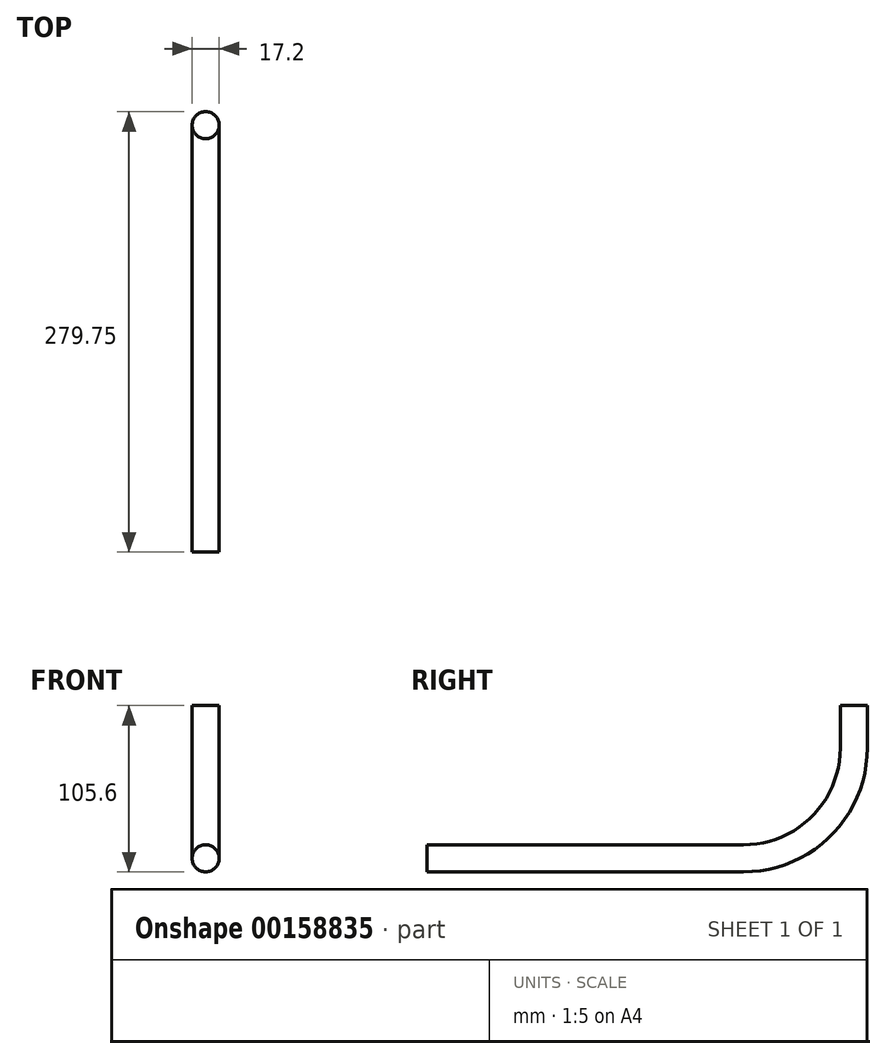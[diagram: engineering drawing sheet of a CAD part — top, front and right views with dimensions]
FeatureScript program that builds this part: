
annotation { "Feature Type Name" : "Feature", "Feature Type Description" : "" }
export const myFeature = defineFeature(function(context is Context, id is Id, definition is map)
    precondition{}
    {
        {
            var Q0;
            Q0=qCreatedBy(makeId("Right.planeOp"),FACE);
            var sketch = newSketch(context, id + "F0", { "sketchPlane" : qUnion([Q0])});
            skLineSegment(sketch, "E0", {"start": v(0, 0) * mm, "end": v(0, -27) * mm});
            skLineSegment(sketch, "E1", {"start": v(-70, -97) * mm, "end": v(-271.15, -97) * mm});
            skPoint(sketch, "E2.visualSharp", {"position": v(0, -97) * mm});
            skArc(sketch, "E2.filletArc", {"start": v(-70, -97) * mm, "mid": v(-20.5, -76.5) * mm, "end": v(0, -27) * mm});
            skSolve(sketch);
        }
        {
            var Q0;
            Q0=qCreatedBy(makeId("Top.planeOp"),FACE);
            var sketch = newSketch(context, id + "F1", { "sketchPlane" : qUnion([Q0])});
            skCircle(sketch, "E3", {"center": v(0, 0) * mm, "radius": 8.6 * mm});
            skSolve(sketch);
        }
        {
            var Q0;
            Q0=makeQuery(id+"F1.imprint","IMPRINT",FACE,{"disambiguationData":[TD([[makeQuery(id+"F1.imprint","IMPRINT",EDGE,{"derivedFrom":sQuery(id+"F1.wireOp",EDGE,"E3")}),1.0]])]});
            var Q1;
            Q1=sQuery(id+"F0.wireOp",EDGE,"E0");
            var Q2;
            Q2=sQuery(id+"F0.wireOp",EDGE,"E2.filletArc");
            var Q3;
            Q3=sQuery(id+"F0.wireOp",EDGE,"E1");
            sweep(context, id + "F2", {"profiles" : qUnion([Q0]), "path" : qUnion([Q1, Q2, Q3])});
        }
    });
